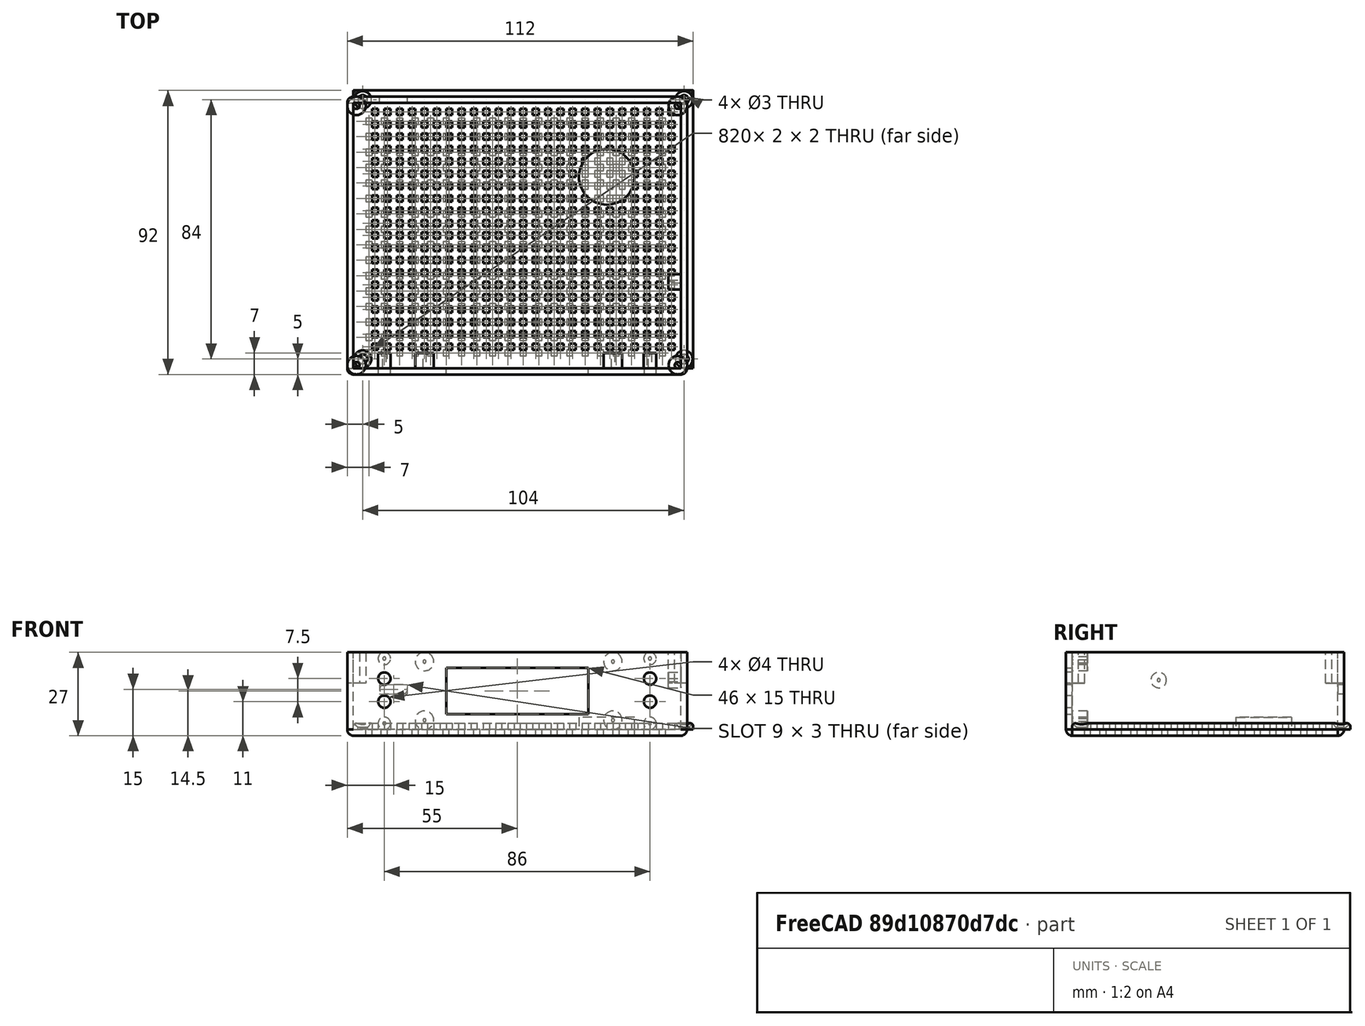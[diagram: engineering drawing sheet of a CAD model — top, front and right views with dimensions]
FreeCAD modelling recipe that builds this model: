
FCSTD DOCUMENT  (FreeCAD 1.0R39109 (Git))
Label: Clock6
License: All rights reserved
LicenseURL: https://en.wikipedia.org/wiki/All_rights_reserved
objects: Sketcher::SketchObject×10, PartDesign::Pocket×5, PartDesign::LinearPattern×4, Part::Extrusion×4, PartDesign::MultiTransform×2, Part::Compound×2, PartDesign::Body×2, Mesh::Feature×2, Part::Box×1, Part::Thickness×1, PartDesign::FeatureBase×1, PartDesign::Pad×1, PartDesign::Fillet×1, PartDesign::Chamfer×1
note: 68 computed .brp shape members not serialized (recipe doc carries the construction recipe); baked Part::Feature solids carry a one-line shape summary decoded from their .brp

FEATURE [Part::Box] Box  label="Куб"
  AttacherType = Attacher::AttachEngine3D
  Height = 25
  Length = 106
  Width = 86
FEATURE [Part::Thickness] Thickness
  Faces = -> Box [Face6]
  Intersection = false
  Join = 0
  Mode = 0
  SelfIntersection = false
  Value = 2
FEATURE [PartDesign::FeatureBase] BaseFeature
  BaseFeature = -> Thickness
  Suppressed = false
FEATURE [Sketcher::SketchObject] Sketch
  ArcFitTolerance = 1e-06
  AttachmentSupport = -> [BaseFeature]
  FullyConstrained = true
  MakeInternals = false
  MapMode = 5
  Placement = pos=(0,0,-2) rot=(1,0,0;3.14159rad)
  sketch-geometry (4):
    g0: LineSegment StartX=4 StartY=-4 StartZ=0 EndX=4 EndY=-6 EndZ=0
    g1: LineSegment StartX=4 StartY=-6 StartZ=0 EndX=6 EndY=-6 EndZ=0
    g2: LineSegment StartX=6 StartY=-6 StartZ=0 EndX=6 EndY=-4 EndZ=0
    g3: LineSegment StartX=6 StartY=-4 StartZ=0 EndX=4 EndY=-4 EndZ=0
  constraints (12):
    c: Coincident(g0,g1)
    c: Coincident(g1,g2)
    c: Coincident(g2,g3)
    c: Coincident(g3,g0)
    c: Vertical(g0)
    c: Vertical(g2)
    c: Horizontal(g1)
    c: Horizontal(g3)
    c: Distance(g0,g2) = 2
    c: Distance(g1,g3) = 2
    c: Distance(g0,g-2) = 4
    c: DistanceY(g0,g-1) = 4
FEATURE [PartDesign::Pocket] Pocket
  BaseFeature = -> BaseFeature
  Direction = (0,0,1)
  Length = 5
  Length2 = 5
  Profile = -> Sketch
  ReferenceAxis = -> Sketch [N_Axis]
  Refine = true
  Suppressed = false
  Type = 1
FEATURE [PartDesign::LinearPattern] LinearPattern
  Direction = -> X_Axis001
  Length = 95
  Mode = 1
  Occurrences = 20
  Offset = 5
  Refine = true
  Suppressed = false
  TransformMode = 0
FEATURE [PartDesign::LinearPattern] LinearPattern001
  Direction = -> Y_Axis001
  Length = 75
  Mode = 1
  Occurrences = 16
  Offset = 5
  Refine = true
  Suppressed = false
  TransformMode = 0
FEATURE [PartDesign::MultiTransform] MultiTransform
  BaseFeature = -> Pocket
  Originals = -> [Pocket]
  Refine = true
  Suppressed = false
  TransformMode = 0
  Transformations = -> [LinearPattern,LinearPattern001]
FEATURE [Sketcher::SketchObject] Sketch001
  ArcFitTolerance = 1e-06
  AttachmentSupport = -> [MultiTransform]
  FullyConstrained = true
  MakeInternals = false
  MapMode = 5
  Placement = pos=(0,-2,0) rot=(1,0,0;1.5708rad)
  sketch-geometry (8):
    g0: LineSegment StartX=30 StartY=20 StartZ=0 EndX=30 EndY=5 EndZ=0
    g1: LineSegment StartX=30 StartY=5 StartZ=0 EndX=76 EndY=5 EndZ=0
    g2: LineSegment StartX=76 StartY=5 StartZ=0 EndX=76 EndY=20 EndZ=0
    g3: LineSegment StartX=76 StartY=20 StartZ=0 EndX=30 EndY=20 EndZ=0
    g4: Circle CenterX=10 CenterY=9 CenterZ=0 NormalX=0 NormalY=0 NormalZ=1 AngleXU=0 Radius=2
    g5: Circle CenterX=10 CenterY=16.5 CenterZ=0 NormalX=0 NormalY=0 NormalZ=1 AngleXU=0 Radius=2
    g6: Circle CenterX=96 CenterY=16.5 CenterZ=0 NormalX=0 NormalY=0 NormalZ=1 AngleXU=0 Radius=2
    g7: Circle CenterX=96 CenterY=9 CenterZ=0 NormalX=0 NormalY=0 NormalZ=1 AngleXU=0 Radius=2
  constraints (24):
    c: Coincident(g0,g1)
    c: Coincident(g1,g2)
    c: Coincident(g2,g3)
    c: Coincident(g3,g0)
    c: Vertical(g0)
    c: Vertical(g2)
    c: Horizontal(g1)
    c: Horizontal(g3)
    c: DistanceX(g-1,g0) = 30
    c: Distance(g0,g-1) = 5
    c: DistanceY(g0,g0) = 15
    c: DistanceX(g0,g2) = 46
    c: Diameter(g4) = 4
    c: Diameter(g5) = 4
    c: Diameter(g6) = 4
    c: Diameter(g7) = 4
    c: DistanceX(g-1,g4) = 10
    c: Vertical(g5,g4)
    c: Horizontal(g7,g4)
    c: Vertical(g6,g7)
    c: Horizontal(g6,g5)
    c: DistanceY(g-1,g4) = 9
    c: DistanceY(g4,g5) = 7.5
    c: DistanceX(g-1,g7) = 96
FEATURE [PartDesign::Pocket] Pocket001
  BaseFeature = -> MultiTransform
  Direction = (0,1,-2e-16)
  Length = 2
  Length2 = 5
  Profile = -> Sketch001
  ReferenceAxis = -> Sketch001 [N_Axis]
  Refine = true
  Suppressed = false
  Type = 0
FEATURE [Sketcher::SketchObject] Sketch002
  ArcFitTolerance = 1e-06
  AttachmentSupport = -> [Pocket001]
  FullyConstrained = true
  MakeInternals = false
  MapMode = 5
  Placement = pos=(0,0,0) rot=(0,0.707107,0.707107;3.14159rad)
  sketch-geometry (16):
    g0: Circle CenterX=-10 CenterY=2 CenterZ=0 NormalX=0 NormalY=0 NormalZ=1 AngleXU=0 Radius=0.5
    g1: Circle CenterX=-10 CenterY=2 CenterZ=0 NormalX=0 NormalY=0 NormalZ=1 AngleXU=0 Radius=2
    g2: Circle CenterX=-23 CenterY=3 CenterZ=0 NormalX=0 NormalY=0 NormalZ=1 AngleXU=0 Radius=0.5
    g3: Circle CenterX=-23 CenterY=22 CenterZ=0 NormalX=0 NormalY=0 NormalZ=1 AngleXU=0 Radius=0.5
    g4: Circle CenterX=-23 CenterY=3 CenterZ=0 NormalX=0 NormalY=0 NormalZ=1 AngleXU=0 Radius=3
    g5: Circle CenterX=-84 CenterY=3 CenterZ=0 NormalX=0 NormalY=0 NormalZ=1 AngleXU=0 Radius=0.5
    g6: Circle CenterX=-84 CenterY=22 CenterZ=0 NormalX=0 NormalY=0 NormalZ=1 AngleXU=0 Radius=0.5
    g7: Circle CenterX=-23 CenterY=22 CenterZ=0 NormalX=0 NormalY=0 NormalZ=1 AngleXU=0 Radius=3
    g8: Circle CenterX=-84 CenterY=22 CenterZ=0 NormalX=0 NormalY=0 NormalZ=1 AngleXU=0 Radius=3
    g9: Circle CenterX=-84 CenterY=3 CenterZ=0 NormalX=0 NormalY=0 NormalZ=1 AngleXU=0 Radius=3
    g10: Circle CenterX=-10 CenterY=23 CenterZ=0 NormalX=0 NormalY=0 NormalZ=1 AngleXU=0 Radius=0.5
    g11: Circle CenterX=-10 CenterY=23 CenterZ=0 NormalX=0 NormalY=0 NormalZ=1 AngleXU=0 Radius=2
    g12: Circle CenterX=-95.9792 CenterY=2 CenterZ=0 NormalX=0 NormalY=0 NormalZ=1 AngleXU=0 Radius=0.5
    g13: Circle CenterX=-95.9792 CenterY=23 CenterZ=0 NormalX=0 NormalY=0 NormalZ=1 AngleXU=0 Radius=0.5
    g14: Circle CenterX=-95.9792 CenterY=2 CenterZ=0 NormalX=0 NormalY=0 NormalZ=1 AngleXU=0 Radius=2
    g15: Circle CenterX=-95.9792 CenterY=23 CenterZ=0 NormalX=0 NormalY=0 NormalZ=1 AngleXU=0 Radius=2
  constraints (40):
    c: Diameter(g0) = 1
    c: Diameter(g1) = 4
    c: Coincident(g1,g0)
    c: DistanceX(g0,g-1) = 10
    c: DistanceY(g-1,g0) = 2
    c: Diameter(g2) = 1
    c: Diameter(g3) = 1
    c: Diameter(g4) = 6
    c: Coincident(g4,g2)
    c: DistanceX(g2,g-1) = 23
    c: DistanceY(g-1,g2) = 3
    c: Diameter(g5) = 1
    c: Diameter(g6) = 1
    c: DistanceX(g5,g-1) = 84
    c: Vertical(g6,g5)
    c: Vertical(g2,g3)
    c: Horizontal(g3,g6)
    c: Horizontal(g5,g2)
    c: Diameter(g7) = 6
    c: Coincident(g7,g3)
    c: Diameter(g8) = 6
    c: Coincident(g8,g6)
    c: Diameter(g9) = 6
    c: Coincident(g9,g5)
    c: DistanceY(g-1,g3) = 22
    c: Diameter(g10) = 1
    c: Diameter(g11) = 4
    c: Coincident(g11,g10)
    c: DistanceY(g-1,g10) = 23
    c: Vertical(g10,g0)
    c: Diameter(g12) = 1
    c: Diameter(g13) = 1
    c: Vertical(g13,g12)
    c: Horizontal(g13,g10)
    c: Horizontal(g0,g12)
    c: Distance(g12,g-1) = 96
    c: Diameter(g14) = 4
    c: Coincident(g14,g12)
    c: Diameter(g15) = 4
    c: Coincident(g15,g13)
FEATURE [Part::Extrusion] Extrude
  Base = -> Sketch002
  Dir = (0,1,-2e-16)
  DirMode = 2
  FaceMakerClass = Part::FaceMakerBullseye
  FaceMakerMode = 3
  LengthFwd = 5
  LengthRev = 0
  Solid = true
  Symmetric = false
FEATURE [Sketcher::SketchObject] Sketch003
  ArcFitTolerance = 1e-06
  AttachmentSupport = -> [Pocket001]
  FullyConstrained = true
  MakeInternals = false
  MapMode = 5
  Placement = pos=(0,88,0) rot=(0,0.707107,0.707107;3.14159rad)
  sketch-geometry (4):
    g0: ArcOfCircle CenterX=-16 CenterY=13 CenterZ=0 NormalX=0 NormalY=0 NormalZ=1 AngleXU=0 Radius=1.5 StartAngle=1.5708 EndAngle=4.71239
    g1: ArcOfCircle CenterX=-10 CenterY=13 CenterZ=0 NormalX=0 NormalY=0 NormalZ=1 AngleXU=0 Radius=1.5 StartAngle=4.71239 EndAngle=7.85398
    g2: LineSegment StartX=-16 StartY=14.5 StartZ=0 EndX=-10 EndY=14.5 EndZ=0
    g3: LineSegment StartX=-16 StartY=11.5 StartZ=0 EndX=-10 EndY=11.5 EndZ=0
  constraints (10):
    c: Tangent(g0,g2) = 1.5708
    c: Tangent(g0,g3) = -1.5708
    c: Tangent(g1,g2) = 1.5708
    c: Tangent(g1,g3) = -1.5708
    c: Equal(g0,g1)
    c: Horizontal(g3)
    c: Distance(g0,g1) = 6
    c: Radius(g0) = 1.5
    c: DistanceX(g1,g-1) = 10
    c: DistanceY(g-1,g1) = 13
FEATURE [Sketcher::SketchObject] Sketch004
  ArcFitTolerance = 1e-06
  FullyConstrained = true
  MakeInternals = false
  MapMode = 5
  sketch-geometry (1):
    g0: Circle CenterX=82 CenterY=62 CenterZ=0 NormalX=0 NormalY=0 NormalZ=1 AngleXU=0 Radius=9
  constraints (3):
    c: Diameter(g0) = 18
    c: DistanceX(g-1,g0) = 82
    c: DistanceY(g-1,g0) = 62
FEATURE [Part::Extrusion] Extrude001
  Base = -> Sketch004
  Dir = (0,0,1)
  DirMode = 2
  FaceMakerClass = Part::FaceMakerBullseye
  FaceMakerMode = 3
  LengthFwd = 4
  LengthRev = 0
  Solid = true
  Symmetric = false
FEATURE [Sketcher::SketchObject] Sketch005
  ArcFitTolerance = 1e-06
  FullyConstrained = true
  MakeInternals = false
  MapMode = 5
  Placement = pos=(106,0,0) rot=(0.57735,-0.57735,-0.57735;2.0944rad)
  sketch-geometry (2):
    g0: Circle CenterX=-28 CenterY=16 CenterZ=0 NormalX=0 NormalY=0 NormalZ=1 AngleXU=0 Radius=0.5
    g1: Circle CenterX=-28 CenterY=16 CenterZ=0 NormalX=0 NormalY=0 NormalZ=1 AngleXU=0 Radius=2.5
  constraints (5):
    c: Diameter(g0) = 1
    c: DistanceY(g-1,g0) = 16
    c: DistanceX(g0,g-1) = 28
    c: Diameter(g1) = 5
    c: Coincident(g1,g0)
FEATURE [Part::Extrusion] Extrude002
  Base = -> Sketch005
  Dir = (-1,0,0)
  DirMode = 2
  FaceMakerClass = Part::FaceMakerBullseye
  FaceMakerMode = 3
  LengthFwd = 4
  LengthRev = 0
  Solid = true
  Symmetric = false
FEATURE [Sketcher::SketchObject] Sketch006
  ArcFitTolerance = 1e-06
  FullyConstrained = true
  MakeInternals = false
  MapMode = 5
  Placement = pos=(0,0,25) rot=(0,0,1;0rad)
  sketch-geometry (8):
    g0: Circle CenterX=1 CenterY=1 CenterZ=0 NormalX=0 NormalY=0 NormalZ=1 AngleXU=0 Radius=1
    g1: Circle CenterX=1 CenterY=1 CenterZ=0 NormalX=0 NormalY=0 NormalZ=1 AngleXU=0 Radius=3
    g2: Circle CenterX=1 CenterY=85 CenterZ=0 NormalX=0 NormalY=0 NormalZ=1 AngleXU=0 Radius=1
    g3: Circle CenterX=1 CenterY=85 CenterZ=0 NormalX=0 NormalY=0 NormalZ=1 AngleXU=0 Radius=3
    g4: Circle CenterX=104.995 CenterY=85 CenterZ=0 NormalX=0 NormalY=0 NormalZ=1 AngleXU=0 Radius=1
    g5: Circle CenterX=104.995 CenterY=85 CenterZ=0 NormalX=0 NormalY=0 NormalZ=1 AngleXU=0 Radius=3
    g6: Circle CenterX=104.995 CenterY=1 CenterZ=0 NormalX=0 NormalY=0 NormalZ=1 AngleXU=0 Radius=1
    g7: Circle CenterX=104.995 CenterY=1 CenterZ=0 NormalX=0 NormalY=0 NormalZ=1 AngleXU=0 Radius=3
  constraints (20):
    c: Diameter(g0) = 2
    c: Diameter(g1) = 6
    c: Coincident(g1,g0)
    c: DistanceY(g-1,g0) = 1
    c: DistanceX(g-1,g0) = 1
    c: Diameter(g2) = 2
    c: DistanceY(g-1,g2) = 85
    c: Diameter(g3) = 6
    c: Coincident(g3,g2)
    c: Vertical(g2,g0)
    c: Diameter(g4) = 2
    c: Diameter(g5) = 6
    c: Coincident(g5,g4)
    c: Diameter(g6) = 2
    c: Diameter(g7) = 6
    c: Coincident(g7,g6)
    c: Vertical(g6,g4)
    c: Horizontal(g4,g2)
    c: Horizontal(g6,g0)
    c: Distance(g6,g-1) = 105
FEATURE [Part::Extrusion] Extrude003
  Base = -> Sketch006
  Dir = (0,0,1)
  DirMode = 2
  FaceMakerClass = Part::FaceMakerBullseye
  FaceMakerMode = 3
  LengthFwd = 10
  LengthRev = 0
  Reversed = true
  Solid = true
  Symmetric = false
FEATURE [Part::Compound] Compound
  Links = -> [Extrude,Extrude001,Extrude002,Extrude003]
FEATURE [PartDesign::Pocket] Pocket002
  BaseFeature = -> Pocket001
  Direction = (0,-1,2e-16)
  Length = 2
  Length2 = 5
  Profile = -> Sketch003
  ReferenceAxis = -> Sketch003 [N_Axis]
  Refine = true
  Suppressed = false
  Type = 0
FEATURE [PartDesign::Body] Body001  label="Тело001"
  AllowCompound = false
  BaseFeature = -> Thickness
  Group = -> [BaseFeature,Sketch,Pocket,MultiTransform,LinearPattern,LinearPattern001,Sketch001,Pocket001,Sketch002,Sketch003,Sketch004,Sketch005,Sketch006,Pocket002]
  Origin = -> Origin001
  Tip = -> Pocket002
FEATURE [Part::Compound] Compound001  label="box"
  Links = -> [Body001,Compound]
FEATURE [Mesh::Feature] Mesh  label="box (Meshed)"
FEATURE [Sketcher::SketchObject] Sketch007
  ArcFitTolerance = 1e-06
  AttachmentSupport = -> [XY_Plane]
  FullyConstrained = true
  MakeInternals = false
  MapMode = 5
  sketch-geometry (4):
    g0: LineSegment StartX=0 StartY=0 StartZ=0 EndX=110 EndY=0 EndZ=0
    g1: LineSegment StartX=110 StartY=0 StartZ=0 EndX=110 EndY=90 EndZ=0
    g2: LineSegment StartX=110 StartY=90 StartZ=0 EndX=0 EndY=90 EndZ=0
    g3: LineSegment StartX=0 StartY=90 StartZ=0 EndX=0 EndY=0 EndZ=0
  constraints (11):
    c: Coincident(g0,g1)
    c: Coincident(g1,g2)
    c: Coincident(g2,g3)
    c: Coincident(g3,g0)
    c: Horizontal(g0)
    c: Horizontal(g2)
    c: Vertical(g1)
    c: Vertical(g3)
    c: Coincident(g0,g-1)
    c: DistanceX(g0,g0) = 110
    c: Distance(g2,g-1) = 90
FEATURE [PartDesign::Pad] Pad
  Direction = (0,0,1)
  Length = 2
  Length2 = 10
  Profile = -> Sketch007
  ReferenceAxis = -> Sketch007 [N_Axis]
  Refine = true
  Suppressed = false
  Type = 0
FEATURE [PartDesign::Fillet] Fillet
  Base = -> Pad [Face6]
  BaseFeature = -> Pad
  Radius = 1
  Refine = true
  SupportTransform = false
  Suppressed = false
  UseAllEdges = false
FEATURE [Sketcher::SketchObject] Sketch008
  ArcFitTolerance = 1e-06
  AttachmentSupport = -> [Fillet]
  FullyConstrained = true
  MakeInternals = false
  MapMode = 5
  Placement = pos=(0,0,2) rot=(0,0,1;0rad)
  sketch-geometry (4):
    g0: Circle CenterX=3 CenterY=3 CenterZ=0 NormalX=0 NormalY=0 NormalZ=1 AngleXU=0 Radius=1.5
    g1: Circle CenterX=107 CenterY=3 CenterZ=0 NormalX=0 NormalY=0 NormalZ=1 AngleXU=0 Radius=1.5
    g2: Circle CenterX=107 CenterY=87 CenterZ=0 NormalX=0 NormalY=0 NormalZ=1 AngleXU=0 Radius=1.5
    g3: Circle CenterX=3 CenterY=87 CenterZ=0 NormalX=0 NormalY=0 NormalZ=1 AngleXU=0 Radius=1.5
  constraints (12):
    c: Diameter(g0) = 3
    c: Diameter(g1) = 3
    c: Diameter(g2) = 3
    c: Diameter(g3) = 3
    c: DistanceY(g-1,g3) = 87
    c: Horizontal(g3,g2)
    c: Vertical(g2,g1)
    c: DistanceX(g-1,g0) = 3
    c: DistanceX(g-1,g1) = 107
    c: Vertical(g3,g0)
    c: Horizontal(g0,g1)
    c: DistanceY(g-1,g0) = 3
FEATURE [PartDesign::Pocket] Pocket003
  BaseFeature = -> Fillet
  Direction = (0,0,-1)
  Length = 2
  Length2 = 5
  Profile = -> Sketch008
  ReferenceAxis = -> Sketch008 [N_Axis]
  Refine = true
  Suppressed = false
  Type = 0
FEATURE [PartDesign::Chamfer] Chamfer
  Angle = 45
  Base = -> Pocket003 [Edge26,Edge27,Edge25,Edge24]
  BaseFeature = -> Pocket003
  ChamferType = 0
  FlipDirection = false
  Refine = true
  Size = 1.3
  Size2 = 1
  SupportTransform = false
  Suppressed = false
  UseAllEdges = false
FEATURE [Sketcher::SketchObject] Sketch009
  ArcFitTolerance = 1e-06
  AttachmentSupport = -> [Chamfer]
  FullyConstrained = true
  MakeInternals = false
  MapMode = 5
  Placement = pos=(0,0,2) rot=(0,0,1;0rad)
  sketch-geometry (4):
    g0: LineSegment StartX=6 StartY=6 StartZ=0 EndX=8 EndY=6 EndZ=0
    g1: LineSegment StartX=8 StartY=6 StartZ=0 EndX=8 EndY=8 EndZ=0
    g2: LineSegment StartX=8 StartY=8 StartZ=0 EndX=6 EndY=8 EndZ=0
    g3: LineSegment StartX=6 StartY=8 StartZ=0 EndX=6 EndY=6 EndZ=0
  constraints (12):
    c: Coincident(g0,g1)
    c: Coincident(g1,g2)
    c: Coincident(g2,g3)
    c: Coincident(g3,g0)
    c: Horizontal(g0)
    c: Horizontal(g2)
    c: Vertical(g1)
    c: Vertical(g3)
    c: Distance(g1,g3) = 2
    c: Distance(g0,g2) = 2
    c: DistanceX(g-1,g0) = 6
    c: DistanceY(g-1,g0) = 6
FEATURE [PartDesign::Pocket] Pocket004
  BaseFeature = -> Chamfer
  Direction = (0,0,-1)
  Length = 2
  Length2 = 5
  Profile = -> Sketch009
  ReferenceAxis = -> Sketch009 [N_Axis]
  Refine = true
  Suppressed = false
  Type = 0
FEATURE [PartDesign::LinearPattern] LinearPattern002
  Direction = -> Sketch009 [H_Axis]
  Length = 96
  Mode = 1
  Occurrences = 25
  Offset = 4
  Refine = true
  Suppressed = false
  TransformMode = 0
FEATURE [PartDesign::LinearPattern] LinearPattern003
  Direction = -> Sketch009 [V_Axis]
  Length = 76
  Mode = 1
  Occurrences = 20
  Offset = 4
  Refine = true
  Suppressed = false
  TransformMode = 0
FEATURE [PartDesign::MultiTransform] MultiTransform001
  BaseFeature = -> Pocket004
  Originals = -> [Pocket004]
  Refine = true
  Suppressed = false
  TransformMode = 0
  Transformations = -> [LinearPattern002,LinearPattern003]
FEATURE [PartDesign::Body] Body  label="cap"
  AllowCompound = false
  Group = -> [Sketch007,Pad,Fillet,Sketch008,Pocket003,Chamfer,Sketch009,Pocket004,MultiTransform001,LinearPattern002,LinearPattern003]
  Origin = -> Origin
  Tip = -> MultiTransform001
FEATURE [Mesh::Feature] Mesh001  label="cap (Meshed)"
